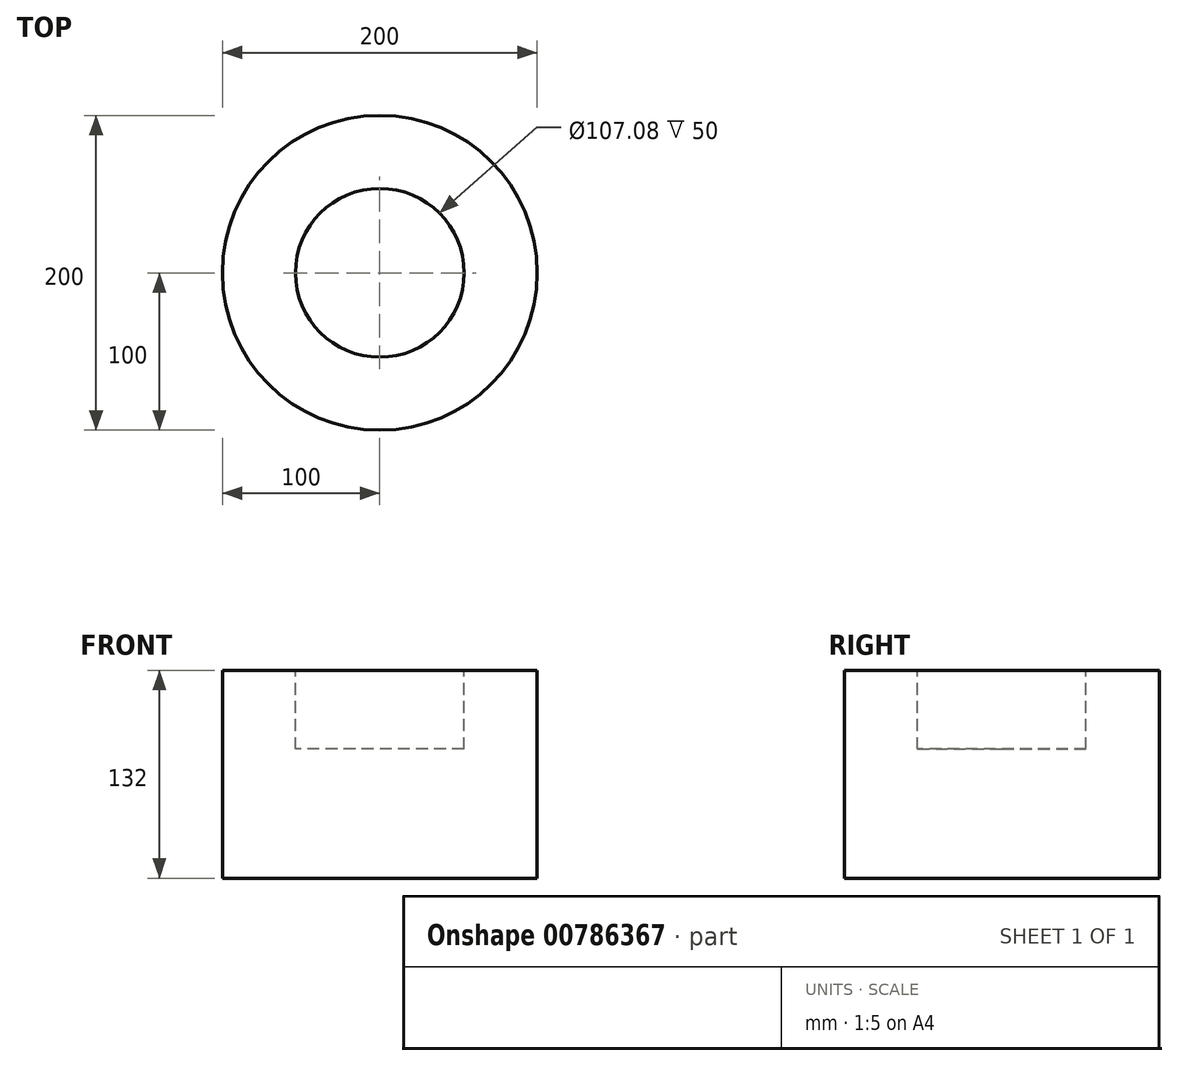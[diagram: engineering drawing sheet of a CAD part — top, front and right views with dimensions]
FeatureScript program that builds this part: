
annotation { "Feature Type Name" : "Feature", "Feature Type Description" : "" }
export const myFeature = defineFeature(function(context is Context, id is Id, definition is map)
    precondition{}
    {
        {
            var Q0;
            Q0=qCreatedBy(makeId("Top.planeOp"),FACE);
            var sketch = newSketch(context, id + "F0", { "sketchPlane" : qUnion([Q0])});
            skCircle(sketch, "E0", {"center": v(0, 0) * mm, "radius": 10 * mm});
            skSolve(sketch);
        }
        {
            var Q0;
            Q0=makeQuery(id+"F0.imprint","IMPRINT",FACE,{"disambiguationData":[TD([[makeQuery(id+"F0.imprint","IMPRINT",EDGE,{"derivedFrom":sQuery(id+"F0.wireOp",EDGE,"E0")}),1.0]])]});
            extrude(context, id + "F1", {"entities" : qUnion([Q0]), "depth" : 25 * mm, "offsetDistance" : 25 * mm});
        }
        {
            var Q0;
            Q0=makeQuery(id+"F1.opExtrude","SWEPT_BODY",BODY,{"disambiguationData":[OSD([sQuery(id+"F0.wireOp",EDGE,"E0")])]});
            deleteBodies(context, id + "F2", {"entities" : qUnion([Q0])});
        }
        {
            var Q0;
            Q0=qCreatedBy(makeId("Top.planeOp"),FACE);
            var sketch = newSketch(context, id + "F3", { "sketchPlane" : qUnion([Q0])});
            skCircle(sketch, "E1", {"center": v(0, 0) * mm, "radius": 100 * mm});
            skSolve(sketch);
        }
        {
            var Q0;
            Q0=makeQuery(id+"F3.imprint","IMPRINT",FACE,{"disambiguationData":[TD([[makeQuery(id+"F3.imprint","IMPRINT",EDGE,{"derivedFrom":sQuery(id+"F3.wireOp",EDGE,"E1")}),1.0]])]});
            extrude(context, id + "F4", {"entities" : qUnion([Q0]), "depth" : 132 * mm, "offsetDistance" : 25 * mm});
        }
        {
            var Q0;
            Q0=makeQuery(id+"F4.opExtrude","CAP_FACE",FACE,{"disambiguationData":[OSD([sQuery(id+"F3.wireOp",EDGE,"E1")])],"isStart":false});
            var sketch = newSketch(context, id + "F5", { "sketchPlane" : qUnion([Q0])});
            skCircle(sketch, "E2", {"center": v(0, 0) * mm, "radius": 53.54 * mm});
            skSolve(sketch);
        }
        {
            var Q0;
            Q0=makeQuery(id+"F5.imprint","IMPRINT",FACE,{"disambiguationData":[TD([[makeQuery(id+"F5.imprint","IMPRINT",EDGE,{"derivedFrom":sQuery(id+"F5.wireOp",EDGE,"E2")}),1.0]])]});
            extrude(context, id + "F6", {"entities" : qUnion([Q0]), "operationType" : NewBodyOperationType.REMOVE, "oppositeDirection" : true, "depth" : 50 * mm, "offsetDistance" : 25 * mm});
        }
    });
